# Revit family: AHUKZ-02B_LC23014
name_source: partatom
category: Aparatos eléctricos
revit_build: Autodesk Revit 2016 (Build: 20150220_1215(x64)
units: mm (PartAtom-declared; Revit-internal decimal feet)

## family parameters
Compartido = No
Corte con vacíos al cargar = No
Cota de conector redondo = Diámetro de uso
Mantener orientación de anotación = No
Número OmniClass = 23.80.00.00
Punto de cálculo de habitación = No
Se basa en plano de trabajo = No
Siempre vertical = Sí
Tipo de pieza = Caja de conexiones
Título OmniClass = Electric Power and Lighting

## types (1)
- AHUKZ-B
    Alimentación = 220-240 ~50Hz / 208-230 ~60 Hz
    Capacidad = 28kW (20,1 ~ 36)
    Costo = 0 $
    Código de montaje = LC23014
    Descripción = CAJAS DE CONTROL COMBINABLE PARA UTA
    Dimensiones = 375 x 350 x 150 mm
    Entrada líquido = 12,7 mm (1/2")
    Fabricante = SALVADOR ESCODA
    Imagen de tipo = ahukz-b.png
    Modelo = AHUKZ-02B
    Salida líquido = 12,7 mm (1/2")
    URL = www.salvadorescoda.com
